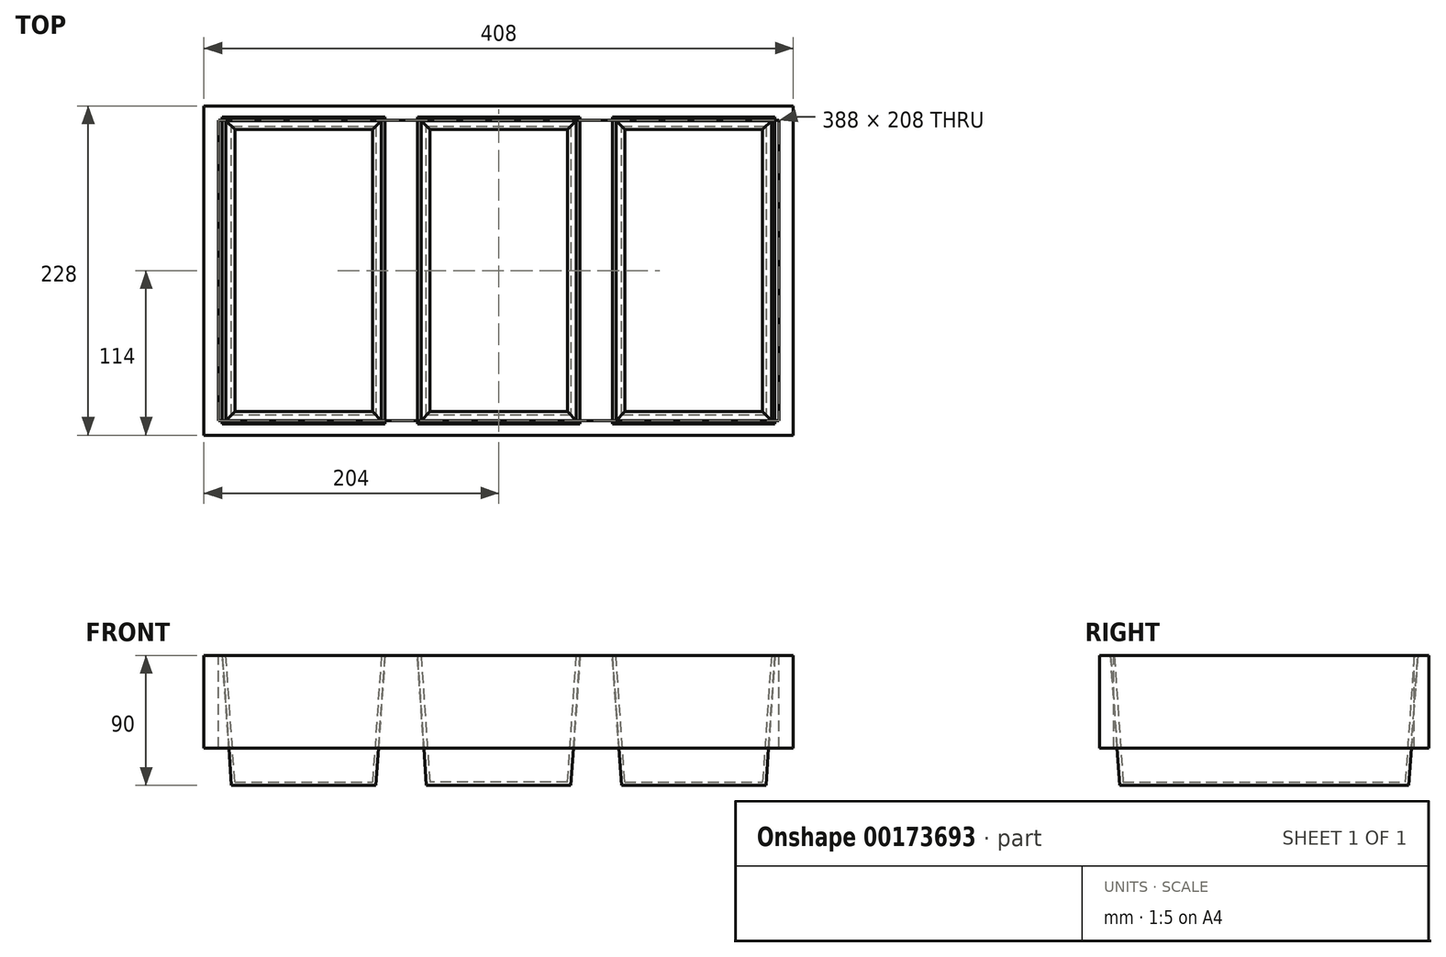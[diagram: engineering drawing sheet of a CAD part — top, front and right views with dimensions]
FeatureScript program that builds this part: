
annotation { "Feature Type Name" : "Feature", "Feature Type Description" : "" }
export const myFeature = defineFeature(function(context is Context, id is Id, definition is map)
    precondition{}
    {
        {
            var Q0;
            Q0=qCreatedBy(makeId("Top.planeOp"),FACE);
            var sketch = newSketch(context, id + "F0", { "sketchPlane" : qUnion([Q0])});
            skLineSegment(sketch, "E0.bottom", {"start": v(50, -100) * mm, "end": v(-50, -100) * mm});
            skLineSegment(sketch, "E0.top", {"start": v(50, 100) * mm, "end": v(-50, 100) * mm});
            skLineSegment(sketch, "E0.left", {"start": v(50, -100) * mm, "end": v(50, 100) * mm});
            skLineSegment(sketch, "E0.right", {"start": v(-50, -100) * mm, "end": v(-50, 100) * mm});
            skPoint(sketch, "E0.middle", {"position": v(0, 0) * mm});
            skLineSegment(sketch, "E1.bottom", {"start": v(85, 100) * mm, "end": v(185, 100) * mm});
            skLineSegment(sketch, "E1.top", {"start": v(85, -100) * mm, "end": v(185, -100) * mm});
            skLineSegment(sketch, "E1.left", {"start": v(85, 100) * mm, "end": v(85, -100) * mm});
            skLineSegment(sketch, "E1.right", {"start": v(185, 100) * mm, "end": v(185, -100) * mm});
            skPoint(sketch, "E1.middle", {"position": v(135, 0) * mm});
            skLineSegment(sketch, "E2.bottom", {"start": v(-185, 100) * mm, "end": v(-85, 100) * mm});
            skLineSegment(sketch, "E2.top", {"start": v(-185, -100) * mm, "end": v(-85, -100) * mm});
            skLineSegment(sketch, "E2.left", {"start": v(-185, 100) * mm, "end": v(-185, -100) * mm});
            skLineSegment(sketch, "E2.right", {"start": v(-85, 100) * mm, "end": v(-85, -100) * mm});
            skPoint(sketch, "E2.middle", {"position": v(-135, 0) * mm});
            skSolve(sketch);
        }
        {
            var Q0;
            Q0=qSketchRegion(id+"F0",true);
            extrude(context, id + "F1", {"entities" : qUnion([Q0]), "depth" : 90 * mm, "hasDraft" : true, "draftAngle" : 4 * degree});
        }
        {
            var Q0;
            Q0=makeQuery(id+"F1.opExtrude","CAP_FACE",FACE,{"disambiguationData":[OSD([sQuery(id+"F0.wireOp",EDGE,"E2.bottom"),sQuery(id+"F0.wireOp",EDGE,"E2.top"),sQuery(id+"F0.wireOp",EDGE,"E2.left"),sQuery(id+"F0.wireOp",EDGE,"E2.right")])],"isStart":false});
            var sketch = newSketch(context, id + "F2", { "sketchPlane" : qUnion([Q0])});
            skLineSegment(sketch, "E3.bottom", {"start": v(194, -104) * mm, "end": v(-194, -104) * mm});
            skLineSegment(sketch, "E3.top", {"start": v(194, 104) * mm, "end": v(-194, 104) * mm});
            skLineSegment(sketch, "E3.left", {"start": v(194, -104) * mm, "end": v(194, 104) * mm});
            skLineSegment(sketch, "E3.right", {"start": v(-194, -104) * mm, "end": v(-194, 104) * mm});
            skPoint(sketch, "E3.middle", {"position": v(0, 0) * mm});
            skLineSegment(sketch, "E4.bottom", {"start": v(204, -114) * mm, "end": v(-204, -114) * mm});
            skLineSegment(sketch, "E4.top", {"start": v(204, 114) * mm, "end": v(-204, 114) * mm});
            skLineSegment(sketch, "E4.left", {"start": v(204, -114) * mm, "end": v(204, 114) * mm});
            skLineSegment(sketch, "E4.right", {"start": v(-204, -114) * mm, "end": v(-204, 114) * mm});
            skSolve(sketch);
        }
        {
            var Q0;
            Q0=qSketchRegion(id+"F2",true);
            extrude(context, id + "F3", {"entities" : qUnion([Q0]), "oppositeDirection" : true, "depth" : 64 * mm});
        }
        {
            var Q0;
            Q0=makeQuery(id+"F1.opExtrude","CAP_FACE",FACE,{"disambiguationData":[OSD([sQuery(id+"F0.wireOp",EDGE,"E2.bottom"),sQuery(id+"F0.wireOp",EDGE,"E2.top"),sQuery(id+"F0.wireOp",EDGE,"E2.left"),sQuery(id+"F0.wireOp",EDGE,"E2.right")])],"isStart":false});
            var Q1;
            Q1=makeQuery(id+"F1.opExtrude","CAP_FACE",FACE,{"disambiguationData":[OSD([sQuery(id+"F0.wireOp",EDGE,"E0.bottom"),sQuery(id+"F0.wireOp",EDGE,"E0.top"),sQuery(id+"F0.wireOp",EDGE,"E0.left"),sQuery(id+"F0.wireOp",EDGE,"E0.right")])],"isStart":false});
            var Q2;
            Q2=makeQuery(id+"F1.opExtrude","CAP_FACE",FACE,{"disambiguationData":[OSD([sQuery(id+"F0.wireOp",EDGE,"E1.bottom"),sQuery(id+"F0.wireOp",EDGE,"E1.top"),sQuery(id+"F0.wireOp",EDGE,"E1.left"),sQuery(id+"F0.wireOp",EDGE,"E1.right")])],"isStart":false});
            shell(context, id + "F4", {"entities" : qUnion([Q0, Q1, Q2]), "thickness" : 2.5 * mm});
        }
    });
